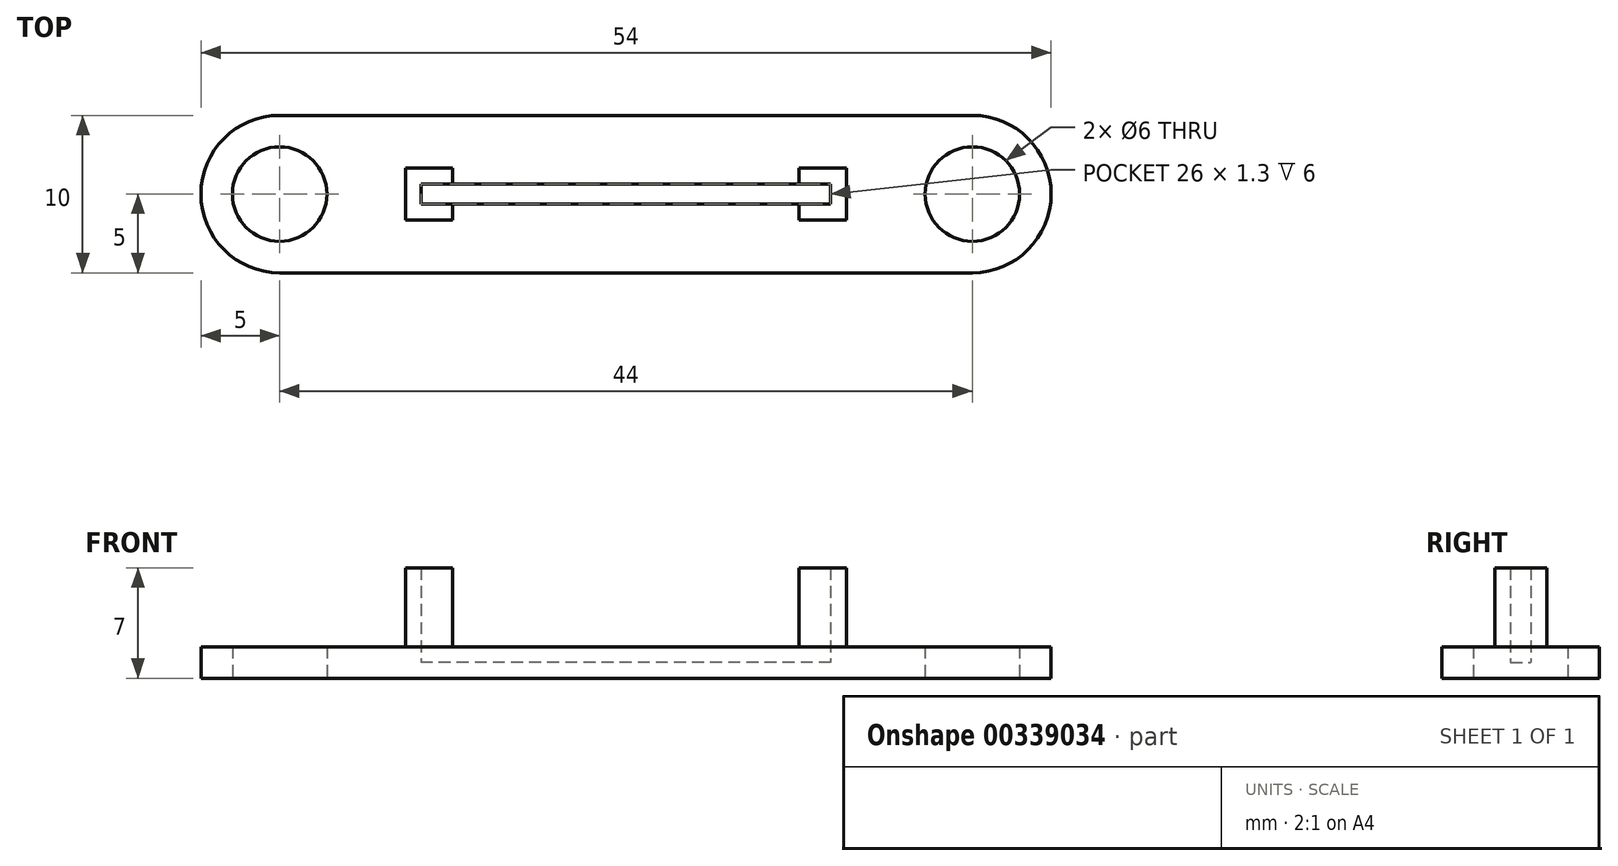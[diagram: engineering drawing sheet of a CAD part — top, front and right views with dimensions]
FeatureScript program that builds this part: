
annotation { "Feature Type Name" : "Feature", "Feature Type Description" : "" }
export const myFeature = defineFeature(function(context is Context, id is Id, definition is map)
    precondition{}
    {
        {
            var Q0;
            Q0=qCreatedBy(makeId("Top.planeOp"),FACE);
            var sketch = newSketch(context, id + "F0", { "sketchPlane" : qUnion([Q0])});
            skCircle(sketch, "E0", {"center": v(31.3, 0) * mm, "radius": 5 * mm});
            skCircle(sketch, "E1", {"center": v(-12.7, 0) * mm, "radius": 5 * mm});
            skLineSegment(sketch, "E2", {"start": v(-12.7, -5) * mm, "end": v(31.3, -5) * mm});
            skLineSegment(sketch, "E3", {"start": v(-12.7, 5) * mm, "end": v(31.3, 5) * mm});
            skCircle(sketch, "E4", {"center": v(-12.7, 0) * mm, "radius": 3 * mm});
            skCircle(sketch, "E5", {"center": v(31.3, 0) * mm, "radius": 3 * mm});
            skSolve(sketch);
        }
        {
            var Q0;
            {var subQ0=sQuery(id+"F0.wireOp",EDGE,"E2");Q0=makeQuery(id+"F0.imprint","IMPRINT",FACE,{"disambiguationData":[TD([[makeQuery(id+"F0.imprint","IMPRINT",EDGE,{"derivedFrom":subQ0}),1.0]])]});}
            var Q1;
            Q1=makeQuery(id+"F0.imprint","IMPRINT",FACE,{"disambiguationData":[TD([[makeQuery(id+"F0.imprint","IMPRINT",EDGE,{"derivedFrom":sQuery(id+"F0.wireOp",EDGE,"E4")}),-1.0]])]});
            var Q2;
            Q2=makeQuery(id+"F0.imprint","IMPRINT",FACE,{"disambiguationData":[TD([[makeQuery(id+"F0.imprint","IMPRINT",EDGE,{"derivedFrom":sQuery(id+"F0.wireOp",EDGE,"E5")}),-1.0]])]});
            extrude(context, id + "F1", {"entities" : qUnion([Q0, Q1, Q2]), "depth" : 2 * mm});
        }
        {
            var Q0;
            Q0=makeQuery(id+"F1.opExtrude","CAP_FACE",FACE,{"disambiguationData":[OSD([sQuery(id+"F0.wireOp",EDGE,"E0"),sQuery(id+"F0.wireOp",EDGE,"E1"),sQuery(id+"F0.wireOp",EDGE,"E2"),sQuery(id+"F0.wireOp",EDGE,"E3"),sQuery(id+"F0.wireOp",EDGE,"E4"),sQuery(id+"F0.wireOp",EDGE,"E5")])],"isStart":false});
            var sketch = newSketch(context, id + "F2", { "sketchPlane" : qUnion([Q0])});
            skLineSegment(sketch, "E6", {"start": v(9.3, 5) * mm, "end": v(9.3, -5) * mm});
            skLineSegment(sketch, "E7", {"start": v(-17.7, 0) * mm, "end": v(26.3, 0) * mm});
            skLineSegment(sketch, "E8.bottom", {"start": v(22.3, -0.65) * mm, "end": v(-3.7, -0.65) * mm});
            skLineSegment(sketch, "E8.top", {"start": v(22.3, 0.65) * mm, "end": v(-3.7, 0.65) * mm});
            skLineSegment(sketch, "E8.left", {"start": v(22.3, -0.65) * mm, "end": v(22.3, 0.65) * mm});
            skLineSegment(sketch, "E8.right", {"start": v(-3.7, -0.65) * mm, "end": v(-3.7, 0.65) * mm});
            skPoint(sketch, "E8.middle", {"position": v(9.3, 0) * mm});
            skLineSegment(sketch, "E9.bottom", {"start": v(23.3, -1.65) * mm, "end": v(-4.7, -1.65) * mm});
            skLineSegment(sketch, "E9.top", {"start": v(23.3, 1.65) * mm, "end": v(-4.7, 1.65) * mm});
            skLineSegment(sketch, "E9.left", {"start": v(23.3, -1.65) * mm, "end": v(23.3, 1.65) * mm});
            skLineSegment(sketch, "E9.right", {"start": v(-4.7, -1.65) * mm, "end": v(-4.7, 1.65) * mm});
            skLineSegment(sketch, "E10", {"start": v(-1.7, 5) * mm, "end": v(-1.7, -5) * mm});
            skLineSegment(sketch, "E11", {"start": v(20.3, -5) * mm, "end": v(20.3, 5) * mm});
            skSolve(sketch);
        }
        {
            var Q0;
            {var subQ0=sQuery(id+"F2.wireOp",EDGE,"E9.right");var subQ8=sQuery(id+"F2.wireOp",EDGE,"E7");var subQ11=makeQuery(id+"F2.imprint","INTERSECT",VERTEX,{"derivedFrom":[subQ8,subQ0]});Q0=makeQuery(id+"F2.imprint","IMPRINT",FACE,{"disambiguationData":[TD([[makeQuery(id+"F2.imprint","IMPRINT",EDGE,{"disambiguationData":[TD([[subQ11,-1.0]])],"derivedFrom":subQ8}),-1.0]])]});}
            var Q1;
            {var subQ3=sQuery(id+"F2.wireOp",EDGE,"E7");var subQ7=sQuery(id+"F2.wireOp",EDGE,"E9.right");var subQ11=makeQuery(id+"F2.imprint","INTERSECT",VERTEX,{"derivedFrom":[subQ3,subQ7]});Q1=makeQuery(id+"F2.imprint","IMPRINT",FACE,{"disambiguationData":[TD([[makeQuery(id+"F2.imprint","IMPRINT",EDGE,{"disambiguationData":[TD([[subQ11,-1.0]])],"derivedFrom":subQ3}),1.0]])]});}
            var Q2;
            {var subQ0=sQuery(id+"F2.wireOp",EDGE,"E9.left");var subQ8=sQuery(id+"F2.wireOp",EDGE,"E7");var subQ11=makeQuery(id+"F2.imprint","INTERSECT",VERTEX,{"derivedFrom":[subQ8,subQ0]});Q2=makeQuery(id+"F2.imprint","IMPRINT",FACE,{"disambiguationData":[TD([[makeQuery(id+"F2.imprint","IMPRINT",EDGE,{"disambiguationData":[TD([[subQ11,1.0]])],"derivedFrom":subQ8}),1.0]])]});}
            var Q3;
            {var subQ0=sQuery(id+"F2.wireOp",EDGE,"E9.left");var subQ8=sQuery(id+"F2.wireOp",EDGE,"E7");var subQ11=makeQuery(id+"F2.imprint","INTERSECT",VERTEX,{"derivedFrom":[subQ8,subQ0]});Q3=makeQuery(id+"F2.imprint","IMPRINT",FACE,{"disambiguationData":[TD([[makeQuery(id+"F2.imprint","IMPRINT",EDGE,{"disambiguationData":[TD([[subQ11,1.0]])],"derivedFrom":subQ8}),-1.0]])]});}
            extrude(context, id + "F3", {"entities" : qUnion([Q0, Q1, Q2, Q3]), "operationType" : NewBodyOperationType.ADD, "depth" : 5 * mm});
        }
        {
            var Q0;
            {var subQ0=sQuery(id+"F2.wireOp",EDGE,"E7");var subQ1=sQuery(id+"F2.wireOp",EDGE,"E6");var subQ2=makeQuery(id+"F2.imprint","INTERSECT",VERTEX,{"derivedFrom":[subQ1,subQ0]});Q0=makeQuery(id+"F2.imprint","IMPRINT",FACE,{"disambiguationData":[TD([[makeQuery(id+"F2.imprint","IMPRINT",EDGE,{"disambiguationData":[TD([[subQ2,-1.0]])],"derivedFrom":subQ1}),-1.0]])]});}
            var Q1;
            {var subQ0=sQuery(id+"F2.wireOp",EDGE,"E8.top");var subQ1=sQuery(id+"F2.wireOp",EDGE,"E6");var subQ2=makeQuery(id+"F2.imprint","INTERSECT",VERTEX,{"derivedFrom":[subQ1,subQ0]});Q1=makeQuery(id+"F2.imprint","IMPRINT",FACE,{"disambiguationData":[TD([[makeQuery(id+"F2.imprint","IMPRINT",EDGE,{"disambiguationData":[TD([[subQ2,-1.0]])],"derivedFrom":subQ1}),-1.0]])]});}
            var Q2;
            {var subQ0=sQuery(id+"F2.wireOp",EDGE,"E8.right");var subQ1=sQuery(id+"F2.wireOp",EDGE,"E7");var subQ2=makeQuery(id+"F2.imprint","INTERSECT",VERTEX,{"derivedFrom":[subQ1,subQ0]});Q2=makeQuery(id+"F2.imprint","IMPRINT",FACE,{"disambiguationData":[TD([[makeQuery(id+"F2.imprint","IMPRINT",EDGE,{"disambiguationData":[TD([[subQ2,-1.0]])],"derivedFrom":subQ1}),-1.0]])]});}
            var Q3;
            {var subQ0=sQuery(id+"F2.wireOp",EDGE,"E8.right");var subQ1=sQuery(id+"F2.wireOp",EDGE,"E7");var subQ2=makeQuery(id+"F2.imprint","INTERSECT",VERTEX,{"derivedFrom":[subQ1,subQ0]});Q3=makeQuery(id+"F2.imprint","IMPRINT",FACE,{"disambiguationData":[TD([[makeQuery(id+"F2.imprint","IMPRINT",EDGE,{"disambiguationData":[TD([[subQ2,-1.0]])],"derivedFrom":subQ1}),1.0]])]});}
            var Q4;
            {var subQ0=sQuery(id+"F2.wireOp",EDGE,"E7");var subQ1=sQuery(id+"F2.wireOp",EDGE,"E6");var subQ2=makeQuery(id+"F2.imprint","INTERSECT",VERTEX,{"derivedFrom":[subQ1,subQ0]});Q4=makeQuery(id+"F2.imprint","IMPRINT",FACE,{"disambiguationData":[TD([[makeQuery(id+"F2.imprint","IMPRINT",EDGE,{"disambiguationData":[TD([[subQ2,-1.0]])],"derivedFrom":subQ1}),1.0]])]});}
            var Q5;
            {var subQ0=sQuery(id+"F2.wireOp",EDGE,"E8.top");var subQ1=sQuery(id+"F2.wireOp",EDGE,"E6");var subQ2=makeQuery(id+"F2.imprint","INTERSECT",VERTEX,{"derivedFrom":[subQ1,subQ0]});Q5=makeQuery(id+"F2.imprint","IMPRINT",FACE,{"disambiguationData":[TD([[makeQuery(id+"F2.imprint","IMPRINT",EDGE,{"disambiguationData":[TD([[subQ2,-1.0]])],"derivedFrom":subQ1}),1.0]])]});}
            var Q6;
            {var subQ0=sQuery(id+"F2.wireOp",EDGE,"E11");var subQ1=sQuery(id+"F2.wireOp",EDGE,"E7");var subQ2=makeQuery(id+"F2.imprint","INTERSECT",VERTEX,{"derivedFrom":[subQ1,subQ0]});Q6=makeQuery(id+"F2.imprint","IMPRINT",FACE,{"disambiguationData":[TD([[makeQuery(id+"F2.imprint","IMPRINT",EDGE,{"disambiguationData":[TD([[subQ2,-1.0]])],"derivedFrom":subQ1}),-1.0]])]});}
            var Q7;
            {var subQ0=sQuery(id+"F2.wireOp",EDGE,"E11");var subQ1=sQuery(id+"F2.wireOp",EDGE,"E7");var subQ2=makeQuery(id+"F2.imprint","INTERSECT",VERTEX,{"derivedFrom":[subQ1,subQ0]});Q7=makeQuery(id+"F2.imprint","IMPRINT",FACE,{"disambiguationData":[TD([[makeQuery(id+"F2.imprint","IMPRINT",EDGE,{"disambiguationData":[TD([[subQ2,-1.0]])],"derivedFrom":subQ1}),1.0]])]});}
            extrude(context, id + "F4", {"entities" : qUnion([Q0, Q1, Q2, Q3, Q4, Q5, Q6, Q7]), "operationType" : NewBodyOperationType.REMOVE, "oppositeDirection" : true, "depth" : 1 * mm});
        }
    });
